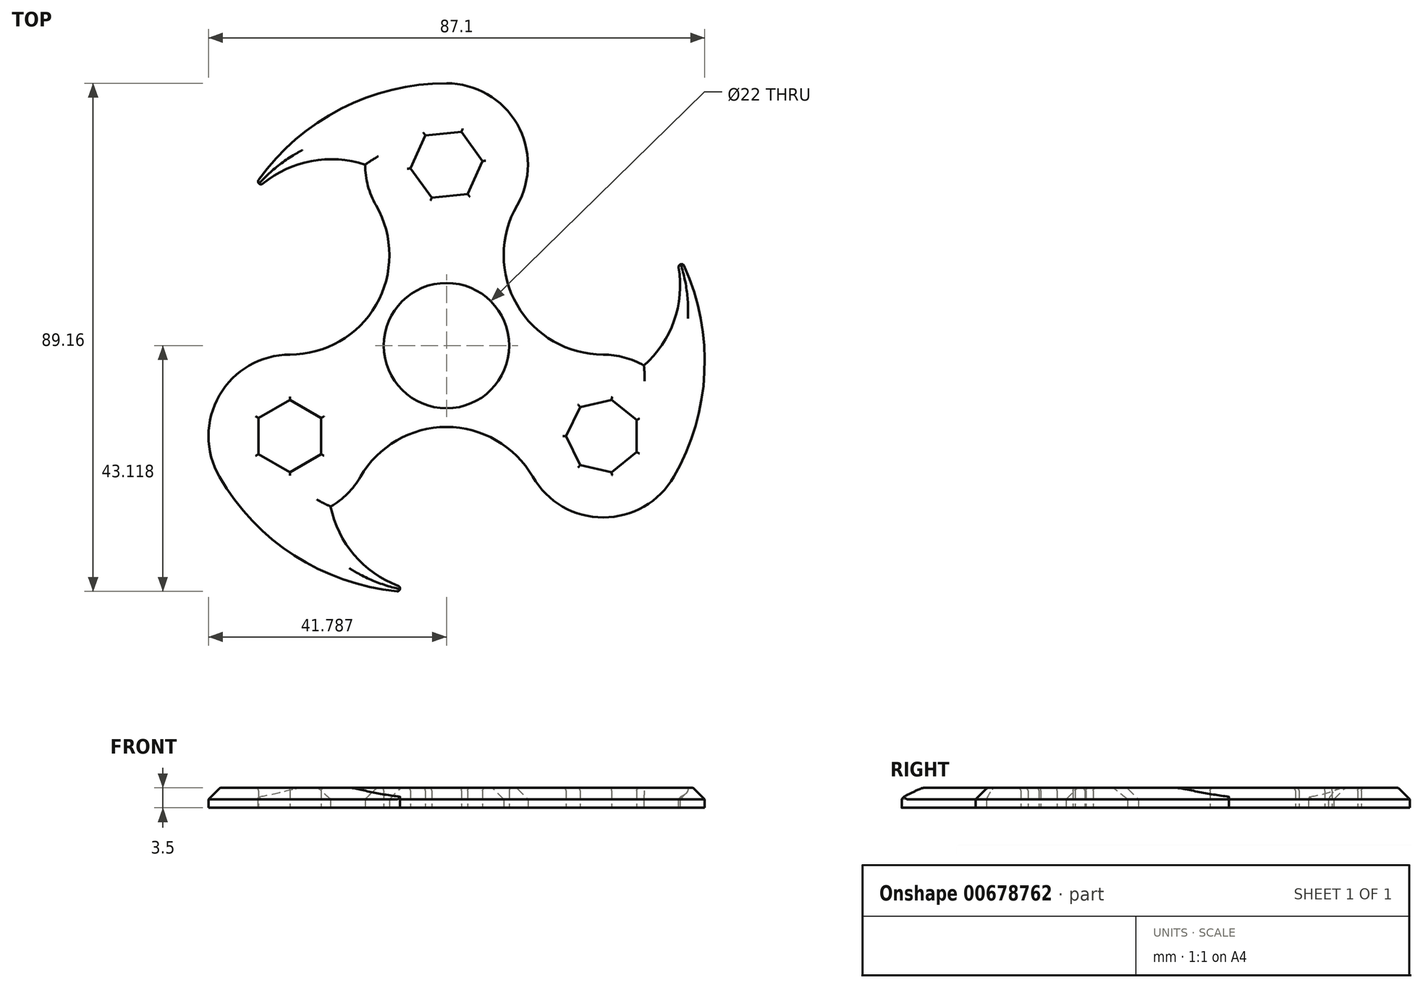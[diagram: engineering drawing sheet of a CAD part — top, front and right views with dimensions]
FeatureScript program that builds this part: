
annotation { "Feature Type Name" : "Feature", "Feature Type Description" : "" }
export const myFeature = defineFeature(function(context is Context, id is Id, definition is map)
    precondition{}
    {
        {
            var Q0;
            Q0=qCreatedBy(makeId("Top.planeOp"),FACE);
            var sketch = newSketch(context, id + "F0", { "sketchPlane" : qUnion([Q0])});
            skArc(sketch, "E0", {"start": v(11.38, 25.11) * mm, "mid": v(11.38, 39.4) * mm, "end": v(-1, 46.55) * mm});
            skCircle(sketch, "E1", {"center": v(-1, 0.5) * mm, "radius": 11 * mm});
            skArc(sketch, "E2.1.1", {"start": v(-28.49, -1.08) * mm, "mid": v(-40.86, -8.22) * mm, "end": v(-40.86, -22.51) * mm});
            skArc(sketch, "E2.2.1", {"start": v(33.65, -3) * mm, "mid": v(30.2, -1.57) * mm, "end": v(26.5, -1.08) * mm});
            skArc(sketch, "E3", {"start": v(-28.49, -1.08) * mm, "mid": v(-13.37, 7.65) * mm, "end": v(-13.37, 25.11) * mm});
            skArc(sketch, "E4.1.0", {"start": v(14.13, -22.51) * mm, "mid": v(-1, -13.78) * mm, "end": v(-16.12, -22.51) * mm});
            skArc(sketch, "E4.2.0", {"start": v(11.38, 25.11) * mm, "mid": v(11.38, 7.65) * mm, "end": v(26.5, -1.08) * mm});
            skArc(sketch, "E5", {"start": v(-1, 46.55) * mm, "mid": v(-21.85, 40.78) * mm, "end": v(-36.78, 25.11) * mm});
            skArc(sketch, "E6", {"start": v(-15.28, 32.26) * mm, "mid": v(-27.22, 32.26) * mm, "end": v(-36.78, 25.11) * mm});
            skPoint(sketch, "E7.center", {"position": v(-2.8, -1.16) * mm});
            skPoint(sketch, "E8.center", {"position": v(0.38, 21.82) * mm});
            skCircle(sketch, "E9.cCircle", {"center": v(26.5, -15.37) * mm, "radius": 5.87 * mm, "construction": true});
            skLineSegment(sketch, "E9.0", {"start": v(32.37, -12.54) * mm, "end": v(32.37, -18.2) * mm});
            skLineSegment(sketch, "E9.1", {"start": v(32.37, -18.2) * mm, "end": v(27.95, -21.72) * mm});
            skLineSegment(sketch, "E9.2", {"start": v(27.95, -21.72) * mm, "end": v(22.44, -20.46) * mm});
            skLineSegment(sketch, "E9.3", {"start": v(22.44, -20.46) * mm, "end": v(20, -15.37) * mm});
            skLineSegment(sketch, "E9.4", {"start": v(20, -15.37) * mm, "end": v(22.44, -10.27) * mm});
            skLineSegment(sketch, "E9.5", {"start": v(22.44, -10.27) * mm, "end": v(27.95, -9.02) * mm});
            skLineSegment(sketch, "E9.6", {"start": v(27.95, -9.02) * mm, "end": v(32.37, -12.54) * mm});
            skPoint(sketch, "E9.0.midPoint", {"position": v(32.37, -15.37) * mm});
            skCircle(sketch, "E10.cCircle", {"center": v(-28.49, -15.37) * mm, "radius": 5.5 * mm, "construction": true});
            skLineSegment(sketch, "E10.0", {"start": v(-33.99, -18.54) * mm, "end": v(-33.99, -12.2) * mm});
            skLineSegment(sketch, "E10.1", {"start": v(-33.99, -12.2) * mm, "end": v(-28.49, -9.02) * mm});
            skLineSegment(sketch, "E10.2", {"start": v(-28.49, -9.02) * mm, "end": v(-22.99, -12.2) * mm});
            skLineSegment(sketch, "E10.3", {"start": v(-22.99, -12.2) * mm, "end": v(-22.99, -18.54) * mm});
            skLineSegment(sketch, "E10.4", {"start": v(-22.99, -18.54) * mm, "end": v(-28.49, -21.72) * mm});
            skLineSegment(sketch, "E10.5", {"start": v(-28.49, -21.72) * mm, "end": v(-33.99, -18.54) * mm});
            skPoint(sketch, "E10.0.midPoint", {"position": v(-33.99, -15.37) * mm});
            skCircle(sketch, "E11.cCircle", {"center": v(-1, 32.26) * mm, "radius": 5.5 * mm, "construction": true});
            skLineSegment(sketch, "E11.0", {"start": v(2.72, 27.1) * mm, "end": v(-3.6, 26.47) * mm});
            skLineSegment(sketch, "E11.1", {"start": v(-3.6, 26.47) * mm, "end": v(-7.31, 31.62) * mm});
            skLineSegment(sketch, "E11.2", {"start": v(-7.31, 31.62) * mm, "end": v(-4.7, 37.4) * mm});
            skLineSegment(sketch, "E11.3", {"start": v(-4.7, 37.4) * mm, "end": v(1.61, 38.05) * mm});
            skLineSegment(sketch, "E11.4", {"start": v(1.61, 38.05) * mm, "end": v(5.32, 32.9) * mm});
            skLineSegment(sketch, "E11.5", {"start": v(5.32, 32.9) * mm, "end": v(2.72, 27.1) * mm});
            skPoint(sketch, "E11.0.midPoint", {"position": v(-0.44, 26.79) * mm});
            skArc(sketch, "E12.trimOffspring", {"start": v(-5.15, 28.62) * mm, "mid": v(-5.13, 28.61) * mm, "end": v(-5.1, 28.6) * mm});
            skPoint(sketch, "E13.orphan", {"position": v(-8.57, -43.72) * mm});
            skPoint(sketch, "E7.2.0.start.orphan", {"position": v(32.37, -7.07) * mm});
            skArc(sketch, "E14.1.0", {"start": v(-40.86, -22.51) * mm, "mid": v(-25.44, -37.69) * mm, "end": v(-4.4, -42.79) * mm});
            skArc(sketch, "E14.1.1", {"start": v(-21.35, -27.74) * mm, "mid": v(-15.38, -38.08) * mm, "end": v(-4.4, -42.79) * mm});
            skArc(sketch, "E14.2.0", {"start": v(38.88, -22.51) * mm, "mid": v(44.31, -1.56) * mm, "end": v(38.21, 19.2) * mm});
            skArc(sketch, "E14.2.1", {"start": v(33.65, -3) * mm, "mid": v(39.62, 7.34) * mm, "end": v(38.21, 19.2) * mm});
            skArc(sketch, "E15.trimOffspring", {"start": v(-15.28, 32.26) * mm, "mid": v(-14.8, 28.56) * mm, "end": v(-13.37, 25.11) * mm});
            skArc(sketch, "E16.trimOffspring", {"start": v(-21.35, -27.74) * mm, "mid": v(-18.39, -25.47) * mm, "end": v(-16.12, -22.51) * mm});
            skArc(sketch, "E17.trimOffspring", {"start": v(14.13, -22.51) * mm, "mid": v(26.5, -29.65) * mm, "end": v(38.88, -22.51) * mm});
            skSolve(sketch);
        }
        {
            var Q0;
            Q0=makeQuery(id+"F0.imprint","IMPRINT",FACE,{"disambiguationData":[TD([[makeQuery(id+"F0.imprint","IMPRINT",EDGE,{"derivedFrom":sQuery(id+"F0.wireOp",EDGE,"E0")}),1.0]])]});
            extrude(context, id + "F1", {"entities" : qUnion([Q0]), "depth" : 3.5 * mm, "offsetDistance" : 25 * mm});
        }
        {
            var Q0;
            Q0=makeQuery(id+"F1.opExtrude","CAP_EDGE",EDGE,{"disambiguationData":[OSD([sQuery(id+"F0.wireOp",EDGE,"E14.1.0")])],"isStart":false});
            var Q1;
            Q1=makeQuery(id+"F1.opExtrude","CAP_EDGE",EDGE,{"disambiguationData":[OSD([sQuery(id+"F0.wireOp",EDGE,"E4.1.0")])],"isStart":false});
            var Q2;
            Q2=makeQuery(id+"F1.opExtrude","CAP_EDGE",EDGE,{"disambiguationData":[OSD([sQuery(id+"F0.wireOp",EDGE,"E17.trimOffspring")])],"isStart":false});
            var Q3;
            Q3=makeQuery(id+"F1.opExtrude","CAP_EDGE",EDGE,{"disambiguationData":[OSD([sQuery(id+"F0.wireOp",EDGE,"E14.1.1")])],"isStart":false});
            var Q4;
            Q4=makeQuery(id+"F1.opExtrude","CAP_EDGE",EDGE,{"disambiguationData":[OSD([sQuery(id+"F0.wireOp",EDGE,"E6")])],"isStart":false});
            var Q5;
            Q5=makeQuery(id+"F1.opExtrude","CAP_EDGE",EDGE,{"disambiguationData":[OSD([sQuery(id+"F0.wireOp",EDGE,"E5")])],"isStart":false});
            var Q6;
            Q6=makeQuery(id+"F1.opExtrude","CAP_EDGE",EDGE,{"disambiguationData":[OSD([sQuery(id+"F0.wireOp",EDGE,"E14.2.1")])],"isStart":false});
            chamfer(context, id + "F2", {"entities" : qUnion([Q0, Q1, Q2, Q3, Q4, Q5, Q6]), "width" : 2 * mm, "tangentPropagation" : true});
        }
        {
            var Q0;
            Q0=makeQuery(id+"F1.opExtrude","CAP_FACE",FACE,{"disambiguationData":[OSD([sQuery(id+"F0.wireOp",EDGE,"E0"),sQuery(id+"F0.wireOp",EDGE,"E1"),sQuery(id+"F0.wireOp",EDGE,"E2.1.1"),sQuery(id+"F0.wireOp",EDGE,"E2.2.1"),sQuery(id+"F0.wireOp",EDGE,"E3"),sQuery(id+"F0.wireOp",EDGE,"E4.1.0"),sQuery(id+"F0.wireOp",EDGE,"E4.2.0"),sQuery(id+"F0.wireOp",EDGE,"E5"),sQuery(id+"F0.wireOp",EDGE,"E6"),sQuery(id+"F0.wireOp",EDGE,"E9.0"),sQuery(id+"F0.wireOp",EDGE,"E9.1"),sQuery(id+"F0.wireOp",EDGE,"E9.2"),sQuery(id+"F0.wireOp",EDGE,"E9.3"),sQuery(id+"F0.wireOp",EDGE,"E9.4"),sQuery(id+"F0.wireOp",EDGE,"E9.5"),sQuery(id+"F0.wireOp",EDGE,"E9.6"),sQuery(id+"F0.wireOp",EDGE,"E10.0"),sQuery(id+"F0.wireOp",EDGE,"E10.1"),sQuery(id+"F0.wireOp",EDGE,"E10.2"),sQuery(id+"F0.wireOp",EDGE,"E10.3"),sQuery(id+"F0.wireOp",EDGE,"E10.4"),sQuery(id+"F0.wireOp",EDGE,"E10.5"),sQuery(id+"F0.wireOp",EDGE,"E11.0"),sQuery(id+"F0.wireOp",EDGE,"E11.1"),sQuery(id+"F0.wireOp",EDGE,"E11.2"),sQuery(id+"F0.wireOp",EDGE,"E11.3"),sQuery(id+"F0.wireOp",EDGE,"E11.4"),sQuery(id+"F0.wireOp",EDGE,"E11.5"),sQuery(id+"F0.wireOp",EDGE,"E14.1.0"),sQuery(id+"F0.wireOp",EDGE,"E14.1.1"),sQuery(id+"F0.wireOp",EDGE,"E14.2.0"),sQuery(id+"F0.wireOp",EDGE,"E14.2.1"),sQuery(id+"F0.wireOp",EDGE,"E15.trimOffspring"),sQuery(id+"F0.wireOp",EDGE,"E16.trimOffspring"),sQuery(id+"F0.wireOp",EDGE,"E17.trimOffspring")])],"isStart":false});
            var Q1;
            Q1=makeQuery(id+"F1.opExtrude","SWEPT_EDGE",EDGE,{"disambiguationData":[OSD([sQuery(id+"F0.wireOp",EDGE,"E5"),sQuery(id+"F0.wireOp",EDGE,"E6")])]});
            var Q2;
            Q2=makeQuery(id+"F1.opExtrude","SWEPT_EDGE",EDGE,{"disambiguationData":[OSD([sQuery(id+"F0.wireOp",EDGE,"E14.1.0"),sQuery(id+"F0.wireOp",EDGE,"E14.1.1")])]});
            var Q3;
            Q3=makeQuery(id+"F1.opExtrude","SWEPT_EDGE",EDGE,{"disambiguationData":[OSD([sQuery(id+"F0.wireOp",EDGE,"E14.2.0"),sQuery(id+"F0.wireOp",EDGE,"E14.2.1")])]});
            fillet(context, id + "F3", {"entities" : qUnion([Q0, Q1, Q2, Q3]), "radius" : .5 * mm, "tangentPropagation" : true, "allowEdgeOverflow" : false});
        }
    });
